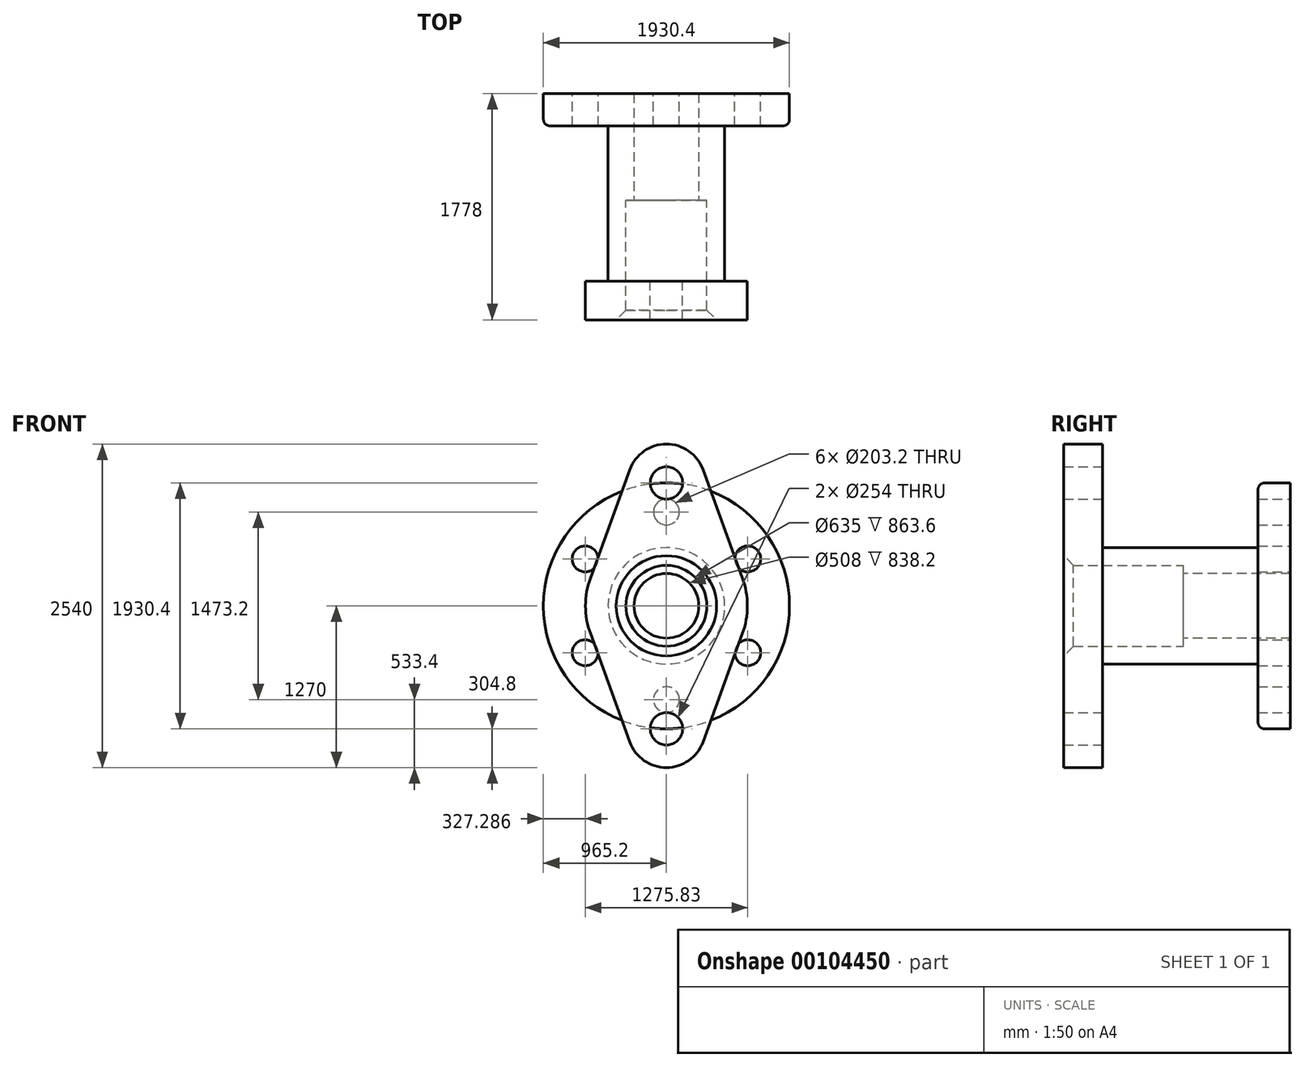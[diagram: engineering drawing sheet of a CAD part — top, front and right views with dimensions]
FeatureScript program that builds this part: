
annotation { "Feature Type Name" : "Feature", "Feature Type Description" : "" }
export const myFeature = defineFeature(function(context is Context, id is Id, definition is map)
    precondition{}
    {
        {
            var Q0;
            Q0=qCreatedBy(makeId("Front.planeOp"),FACE);
            var sketch = newSketch(context, id + "F0", { "sketchPlane" : qUnion([Q0])});
            skCircle(sketch, "E0", {"center": v(0, 0) * mm, "radius": 965.2 * mm});
            skCircle(sketch, "E1", {"center": v(0, 0) * mm, "radius": 736.6 * mm});
            skCircle(sketch, "E2", {"center": v(0, 736.6) * mm, "radius": 101.6 * mm});
            skCircle(sketch, "E3.1.0", {"center": v(-637.91, 368.3) * mm, "radius": 101.6 * mm});
            skCircle(sketch, "E3.2.0", {"center": v(-637.91, -368.3) * mm, "radius": 101.6 * mm});
            skCircle(sketch, "E3.3.0", {"center": v(0, -736.6) * mm, "radius": 101.6 * mm});
            skCircle(sketch, "E3.4.0", {"center": v(637.91, -368.3) * mm, "radius": 101.6 * mm});
            skCircle(sketch, "E3.5.0", {"center": v(637.91, 368.3) * mm, "radius": 101.6 * mm});
            skSolve(sketch);
        }
        {
            var Q0;
            Q0=qSketchRegion(id+"F0",true);
            var Q1;
            {var subQ1=sQuery(id+"F0.wireOp",EDGE,"E1");var subQ4=sQuery(id+"F0.wireOp",EDGE,"E3.7.0");var subQ22=makeQuery(id+"F0.imprint","INTERSECT",VERTEX,{"disambiguationData":[OD(0.0)],"derivedFrom":[subQ1,subQ4]});Q1=makeQuery(id+"F0.imprint","IMPRINT",FACE,{"disambiguationData":[TD([[makeQuery(id+"F0.imprint","IMPRINT",EDGE,{"disambiguationData":[TD([[subQ22,1.0]])],"derivedFrom":subQ1}),1.0]])]});}
            var Q2;
            {var subQ0=sQuery(id+"F0.wireOp",EDGE,"E3.1.0");var subQ1=sQuery(id+"F0.wireOp",EDGE,"E1");var subQ2=makeQuery(id+"F0.imprint","INTERSECT",VERTEX,{"disambiguationData":[OD(0.0)],"derivedFrom":[subQ1,subQ0]});Q2=makeQuery(id+"F0.imprint","IMPRINT",FACE,{"disambiguationData":[TD([[makeQuery(id+"F0.imprint","IMPRINT",EDGE,{"disambiguationData":[TD([[subQ2,-1.0]])],"derivedFrom":subQ1}),-1.0]])]});}
            var Q3;
            {var subQ0=sQuery(id+"F0.wireOp",EDGE,"E3.1.0");var subQ1=sQuery(id+"F0.wireOp",EDGE,"E1");var subQ2=makeQuery(id+"F0.imprint","INTERSECT",VERTEX,{"disambiguationData":[OD(0.0)],"derivedFrom":[subQ1,subQ0]});Q3=makeQuery(id+"F0.imprint","IMPRINT",FACE,{"disambiguationData":[TD([[makeQuery(id+"F0.imprint","IMPRINT",EDGE,{"disambiguationData":[TD([[subQ2,-1.0]])],"derivedFrom":subQ1}),1.0]])]});}
            var Q4;
            {var subQ0=sQuery(id+"F0.wireOp",EDGE,"E2");var subQ1=sQuery(id+"F0.wireOp",EDGE,"E1");var subQ2=makeQuery(id+"F0.imprint","INTERSECT",VERTEX,{"disambiguationData":[OD(0.0)],"derivedFrom":[subQ1,subQ0]});Q4=makeQuery(id+"F0.imprint","IMPRINT",FACE,{"disambiguationData":[TD([[makeQuery(id+"F0.imprint","IMPRINT",EDGE,{"disambiguationData":[TD([[subQ2,-1.0]])],"derivedFrom":subQ1}),-1.0]])]});}
            var Q5;
            {var subQ0=sQuery(id+"F0.wireOp",EDGE,"E2");var subQ1=sQuery(id+"F0.wireOp",EDGE,"E1");var subQ2=makeQuery(id+"F0.imprint","INTERSECT",VERTEX,{"disambiguationData":[OD(0.0)],"derivedFrom":[subQ1,subQ0]});Q5=makeQuery(id+"F0.imprint","IMPRINT",FACE,{"disambiguationData":[TD([[makeQuery(id+"F0.imprint","IMPRINT",EDGE,{"disambiguationData":[TD([[subQ2,-1.0]])],"derivedFrom":subQ1}),1.0]])]});}
            var Q6;
            {var subQ0=sQuery(id+"F0.wireOp",EDGE,"E3.7.0");var subQ1=sQuery(id+"F0.wireOp",EDGE,"E1");var subQ2=makeQuery(id+"F0.imprint","INTERSECT",VERTEX,{"disambiguationData":[OD(0.0)],"derivedFrom":[subQ1,subQ0]});Q6=makeQuery(id+"F0.imprint","IMPRINT",FACE,{"disambiguationData":[TD([[makeQuery(id+"F0.imprint","IMPRINT",EDGE,{"disambiguationData":[TD([[subQ2,-1.0]])],"derivedFrom":subQ1}),-1.0]])]});}
            var Q7;
            {var subQ0=sQuery(id+"F0.wireOp",EDGE,"E3.7.0");var subQ1=sQuery(id+"F0.wireOp",EDGE,"E1");var subQ2=makeQuery(id+"F0.imprint","INTERSECT",VERTEX,{"disambiguationData":[OD(0.0)],"derivedFrom":[subQ1,subQ0]});Q7=makeQuery(id+"F0.imprint","IMPRINT",FACE,{"disambiguationData":[TD([[makeQuery(id+"F0.imprint","IMPRINT",EDGE,{"disambiguationData":[TD([[subQ2,-1.0]])],"derivedFrom":subQ1}),1.0]])]});}
            var Q8;
            {var subQ0=sQuery(id+"F0.wireOp",EDGE,"E3.6.0");var subQ1=sQuery(id+"F0.wireOp",EDGE,"E1");var subQ2=makeQuery(id+"F0.imprint","INTERSECT",VERTEX,{"disambiguationData":[OD(0.0)],"derivedFrom":[subQ1,subQ0]});Q8=makeQuery(id+"F0.imprint","IMPRINT",FACE,{"disambiguationData":[TD([[makeQuery(id+"F0.imprint","IMPRINT",EDGE,{"disambiguationData":[TD([[subQ2,1.0]])],"derivedFrom":subQ1}),-1.0]])]});}
            var Q9;
            {var subQ0=sQuery(id+"F0.wireOp",EDGE,"E3.6.0");var subQ1=sQuery(id+"F0.wireOp",EDGE,"E1");var subQ2=makeQuery(id+"F0.imprint","INTERSECT",VERTEX,{"disambiguationData":[OD(0.0)],"derivedFrom":[subQ1,subQ0]});Q9=makeQuery(id+"F0.imprint","IMPRINT",FACE,{"disambiguationData":[TD([[makeQuery(id+"F0.imprint","IMPRINT",EDGE,{"disambiguationData":[TD([[subQ2,1.0]])],"derivedFrom":subQ1}),1.0]])]});}
            var Q10;
            {var subQ0=sQuery(id+"F0.wireOp",EDGE,"E3.2.0");var subQ1=sQuery(id+"F0.wireOp",EDGE,"E1");var subQ2=makeQuery(id+"F0.imprint","INTERSECT",VERTEX,{"disambiguationData":[OD(0.0)],"derivedFrom":[subQ1,subQ0]});Q10=makeQuery(id+"F0.imprint","IMPRINT",FACE,{"disambiguationData":[TD([[makeQuery(id+"F0.imprint","IMPRINT",EDGE,{"disambiguationData":[TD([[subQ2,-1.0]])],"derivedFrom":subQ1}),1.0]])]});}
            var Q11;
            {var subQ0=sQuery(id+"F0.wireOp",EDGE,"E3.2.0");var subQ1=sQuery(id+"F0.wireOp",EDGE,"E1");var subQ2=makeQuery(id+"F0.imprint","INTERSECT",VERTEX,{"disambiguationData":[OD(0.0)],"derivedFrom":[subQ1,subQ0]});Q11=makeQuery(id+"F0.imprint","IMPRINT",FACE,{"disambiguationData":[TD([[makeQuery(id+"F0.imprint","IMPRINT",EDGE,{"disambiguationData":[TD([[subQ2,-1.0]])],"derivedFrom":subQ1}),-1.0]])]});}
            var Q12;
            {var subQ0=sQuery(id+"F0.wireOp",EDGE,"E3.3.0");var subQ1=sQuery(id+"F0.wireOp",EDGE,"E1");var subQ2=makeQuery(id+"F0.imprint","INTERSECT",VERTEX,{"disambiguationData":[OD(0.0)],"derivedFrom":[subQ1,subQ0]});Q12=makeQuery(id+"F0.imprint","IMPRINT",FACE,{"disambiguationData":[TD([[makeQuery(id+"F0.imprint","IMPRINT",EDGE,{"disambiguationData":[TD([[subQ2,-1.0]])],"derivedFrom":subQ1}),-1.0]])]});}
            var Q13;
            {var subQ0=sQuery(id+"F0.wireOp",EDGE,"E3.3.0");var subQ1=sQuery(id+"F0.wireOp",EDGE,"E1");var subQ2=makeQuery(id+"F0.imprint","INTERSECT",VERTEX,{"disambiguationData":[OD(0.0)],"derivedFrom":[subQ1,subQ0]});Q13=makeQuery(id+"F0.imprint","IMPRINT",FACE,{"disambiguationData":[TD([[makeQuery(id+"F0.imprint","IMPRINT",EDGE,{"disambiguationData":[TD([[subQ2,-1.0]])],"derivedFrom":subQ1}),1.0]])]});}
            var Q14;
            {var subQ0=sQuery(id+"F0.wireOp",EDGE,"E3.4.0");var subQ1=sQuery(id+"F0.wireOp",EDGE,"E1");var subQ2=makeQuery(id+"F0.imprint","INTERSECT",VERTEX,{"disambiguationData":[OD(0.0)],"derivedFrom":[subQ1,subQ0]});Q14=makeQuery(id+"F0.imprint","IMPRINT",FACE,{"disambiguationData":[TD([[makeQuery(id+"F0.imprint","IMPRINT",EDGE,{"disambiguationData":[TD([[subQ2,-1.0]])],"derivedFrom":subQ1}),-1.0]])]});}
            var Q15;
            {var subQ0=sQuery(id+"F0.wireOp",EDGE,"E3.4.0");var subQ1=sQuery(id+"F0.wireOp",EDGE,"E1");var subQ2=makeQuery(id+"F0.imprint","INTERSECT",VERTEX,{"disambiguationData":[OD(0.0)],"derivedFrom":[subQ1,subQ0]});Q15=makeQuery(id+"F0.imprint","IMPRINT",FACE,{"disambiguationData":[TD([[makeQuery(id+"F0.imprint","IMPRINT",EDGE,{"disambiguationData":[TD([[subQ2,-1.0]])],"derivedFrom":subQ1}),1.0]])]});}
            var Q16;
            {var subQ0=sQuery(id+"F0.wireOp",EDGE,"E3.5.0");var subQ1=sQuery(id+"F0.wireOp",EDGE,"E1");var subQ2=makeQuery(id+"F0.imprint","INTERSECT",VERTEX,{"disambiguationData":[OD(0.0)],"derivedFrom":[subQ1,subQ0]});Q16=makeQuery(id+"F0.imprint","IMPRINT",FACE,{"disambiguationData":[TD([[makeQuery(id+"F0.imprint","IMPRINT",EDGE,{"disambiguationData":[TD([[subQ2,-1.0]])],"derivedFrom":subQ1}),-1.0]])]});}
            var Q17;
            {var subQ0=sQuery(id+"F0.wireOp",EDGE,"E3.5.0");var subQ1=sQuery(id+"F0.wireOp",EDGE,"E1");var subQ2=makeQuery(id+"F0.imprint","INTERSECT",VERTEX,{"disambiguationData":[OD(0.0)],"derivedFrom":[subQ1,subQ0]});Q17=makeQuery(id+"F0.imprint","IMPRINT",FACE,{"disambiguationData":[TD([[makeQuery(id+"F0.imprint","IMPRINT",EDGE,{"disambiguationData":[TD([[subQ2,-1.0]])],"derivedFrom":subQ1}),1.0]])]});}
            var Q18;
            {var subQ0=sQuery(id+"F0.wireOp",EDGE,"E3.5.0");var subQ1=sQuery(id+"F0.wireOp",EDGE,"E1");var subQ2=makeQuery(id+"F0.imprint","INTERSECT",VERTEX,{"disambiguationData":[OD(0.0)],"derivedFrom":[subQ1,subQ0]});Q18=makeQuery(id+"F0.imprint","IMPRINT",FACE,{"disambiguationData":[TD([[makeQuery(id+"F0.imprint","IMPRINT",EDGE,{"disambiguationData":[TD([[subQ2,1.0]])],"derivedFrom":subQ1}),1.0]])]});}
            var Q19;
            {var subQ0=sQuery(id+"F0.wireOp",EDGE,"E3.5.0");var subQ1=sQuery(id+"F0.wireOp",EDGE,"E1");var subQ2=makeQuery(id+"F0.imprint","INTERSECT",VERTEX,{"disambiguationData":[OD(0.0)],"derivedFrom":[subQ1,subQ0]});Q19=makeQuery(id+"F0.imprint","IMPRINT",FACE,{"disambiguationData":[TD([[makeQuery(id+"F0.imprint","IMPRINT",EDGE,{"disambiguationData":[TD([[subQ2,1.0]])],"derivedFrom":subQ1}),-1.0]])]});}
            extrude(context, id + "F1", {"entities" : qUnion([Q0, Q1, Q2, Q3, Q4, Q5, Q6, Q7, Q8, Q9, Q10, Q11, Q12, Q13, Q14, Q15, Q16, Q17, Q18, Q19]), "depth" : 254 * mm});
        }
        {
            var Q0;
            Q0=sQuery(id+"F0.wireOp",VERTEX,"E2.center");
            var Q1;
            Q1=sQuery(id+"F0.wireOp",VERTEX,"E3.1.0.center");
            var Q2;
            Q2=sQuery(id+"F0.wireOp",VERTEX,"E3.2.0.center");
            var Q3;
            Q3=sQuery(id+"F0.wireOp",VERTEX,"E3.3.0.center");
            var Q4;
            Q4=sQuery(id+"F0.wireOp",VERTEX,"E3.4.0.center");
            var Q5;
            Q5=sQuery(id+"F0.wireOp",VERTEX,"E3.5.0.center");
            var Q6;
            Q6=makeQuery(id+"F1.opExtrude","SWEPT_BODY",BODY,{"disambiguationData":[OSD([sQuery(id+"F0.wireOp",EDGE,"E0")])]});
            hole(context, id + "F2", {"style" : HoleStyle.SIMPLE, "endStyle" : HoleEndStyle.THROUGH, "oppositeDirection" : true, "holeDiameter" : 203.2 * mm, "locations" : qUnion([Q0, Q1, Q2, Q3, Q4, Q5]), "scope" : qUnion([Q6]), "isTappedThrough" : true});
        }
        {
            var Q0;
            Q0=makeQuery(id+"F1.opExtrude","CAP_FACE",FACE,{"disambiguationData":[OSD([sQuery(id+"F0.wireOp",EDGE,"E0")])],"isStart":false});
            var sketch = newSketch(context, id + "F3", { "sketchPlane" : qUnion([Q0])});
            skCircle(sketch, "E4", {"center": v(0, 0) * mm, "radius": 457.2 * mm});
            skCircle(sketch, "E5", {"center": v(0, 0) * mm, "radius": 254 * mm});
            skCircle(sketch, "E6", {"center": v(0, 0) * mm, "radius": 317.5 * mm});
            skSolve(sketch);
        }
        {
            var Q0;
            Q0=makeQuery(id+"F3.imprint","IMPRINT",FACE,{"disambiguationData":[TD([[makeQuery(id+"F3.imprint","IMPRINT",EDGE,{"derivedFrom":sQuery(id+"F3.wireOp",EDGE,"E4")}),1.0]])]});
            extrude(context, id + "F4", {"entities" : qUnion([Q0]), "operationType" : NewBodyOperationType.ADD, "depth" : 1219.2 * mm});
        }
        {
            var Q0;
            Q0=makeQuery(id+"F1.opExtrude","CAP_EDGE",EDGE,{"disambiguationData":[OSD([sQuery(id+"F0.wireOp",EDGE,"E0")])],"isStart":false});
            var Q1;
            Q1=makeQuery(id+"F4.opExtrude","CAP_EDGE",EDGE,{"disambiguationData":[OSD([sQuery(id+"F3.wireOp",EDGE,"E4")])],"isStart":true});
            fillet(context, id + "F5", {"entities" : qUnion([Q0, Q1]), "radius" : 50.8 * mm, "tangentPropagation" : true, "allowEdgeOverflow" : false});
        }
        {
            var Q0;
            Q0=makeQuery(id+"F3.imprint","IMPRINT",FACE,{"disambiguationData":[TD([[makeQuery(id+"F3.imprint","IMPRINT",EDGE,{"derivedFrom":sQuery(id+"F3.wireOp",EDGE,"E5")}),1.0]])]});
            extrude(context, id + "F6", {"entities" : qUnion([Q0]), "operationType" : NewBodyOperationType.REMOVE, "endBound" : BoundingType.THROUGH_ALL, "oppositeDirection" : true, "depth" : 2540 * mm});
        }
        {
            var Q0;
            Q0=makeQuery(id+"F3.imprint","IMPRINT",FACE,{"disambiguationData":[TD([[makeQuery(id+"F3.imprint","IMPRINT",EDGE,{"derivedFrom":sQuery(id+"F3.wireOp",EDGE,"E5")}),-1.0]])]});
            extrude(context, id + "F7", {"entities" : qUnion([Q0]), "operationType" : NewBodyOperationType.ADD, "depth" : 584.2 * mm});
        }
        {
            var Q0;
            Q0=makeQuery(id+"F4.opExtrude","CAP_FACE",FACE,{"disambiguationData":[OSD([sQuery(id+"F3.wireOp",EDGE,"E4"),sQuery(id+"F3.wireOp",EDGE,"E6")])],"isStart":false});
            var sketch = newSketch(context, id + "F8", { "sketchPlane" : qUnion([Q0])});
            skLineSegment(sketch, "E7", {"start": v(0, 0) * mm, "end": v(0, 2027.99) * mm});
            skLineSegment(sketch, "E8", {"start": v(0, 0) * mm, "end": v(0, -1830.79) * mm});
            skLineSegment(sketch, "E9", {"start": v(0, 0) * mm, "end": v(-1579.68, 0) * mm});
            skLineSegment(sketch, "E10", {"start": v(0, 0) * mm, "end": v(2023.02, 0) * mm});
            skSolve(sketch);
        }
        {
            var Q0;
            {var subQ0=sQuery(id+"F8.wireOp",EDGE,"E7");var subQ1=makeQuery(id+"F4.opExtrude","CAP_EDGE",EDGE,{"disambiguationData":[OSD([sQuery(id+"F3.wireOp",EDGE,"E4")])],"isStart":false});var subQ2=makeQuery(id+"F8.imprint","INTERSECT",VERTEX,{"derivedFrom":[subQ1,subQ0]});Q0=makeQuery(id+"F8.imprint","IMPRINT",FACE,{"disambiguationData":[TD([[makeQuery(id+"F8.imprint","IMPRINT",EDGE,{"disambiguationData":[TD([[subQ2,1.0]])],"derivedFrom":subQ0}),1.0]])]});}
            var sketch = newSketch(context, id + "F9", { "sketchPlane" : qUnion([Q0])});
            skPoint(sketch, "E11", {"position": v(0, 965.2) * mm});
            skPoint(sketch, "E12", {"position": v(0, -965.2) * mm});
            skCircle(sketch, "E13", {"center": v(0, 965.2) * mm, "radius": 304.8 * mm});
            skCircle(sketch, "E14", {"center": v(0, 965.2) * mm, "radius": 127 * mm});
            skCircle(sketch, "E15", {"center": v(0, -965.2) * mm, "radius": 304.8 * mm});
            skCircle(sketch, "E16", {"center": v(0, -965.2) * mm, "radius": 127 * mm});
            skCircle(sketch, "E17", {"center": v(0, 0) * mm, "radius": 279.4 * mm});
            skCircle(sketch, "E18", {"center": v(0, 0) * mm, "radius": 330.2 * mm});
            skCircle(sketch, "E19", {"center": v(0, 0) * mm, "radius": 635 * mm});
            skLineSegment(sketch, "E20", {"start": v(286.4, 1069.47) * mm, "end": v(597.58, 214.77) * mm});
            skLineSegment(sketch, "E21", {"start": v(596.69, -217.24) * mm, "end": v(248.85, -1172.62) * mm});
            skLineSegment(sketch, "E22", {"start": v(0, 965.2) * mm, "end": v(0, -965.2) * mm});
            skLineSegment(sketch, "E23", {"start": v(-286.4, -1069.47) * mm, "end": v(-675.78, 0) * mm});
            skLineSegment(sketch, "E24", {"start": v(-286.4, 1069.47) * mm, "end": v(-596.69, 217.24) * mm});
            skSolve(sketch);
        }
        {
            var Q0;
            {var subQ13=sQuery(id+"F9.wireOp",EDGE,"ya8A9BkE-coIV-0aEf-c29y-W11fJcQt8qWr");Q0=makeQuery(id+"F9.imprint","IMPRINT",FACE,{"disambiguationData":[TD([[makeQuery(id+"F9.imprint","IMPRINT",EDGE,{"derivedFrom":subQ13}),-1.0]])]});}
            var Q1;
            {var subQ1=sQuery(id+"F8.wireOp",EDGE,"E7");var subQ2=makeQuery(id+"F4.opExtrude","CAP_EDGE",EDGE,{"disambiguationData":[OSD([sQuery(id+"F3.wireOp",EDGE,"E4")])],"isStart":false});var subQ3=makeQuery(id+"F8.imprint","INTERSECT",VERTEX,{"derivedFrom":[subQ2,subQ1]});var subQ11=makeQuery(id+"F8.imprint","IMPRINT",EDGE,{"disambiguationData":[TD([[subQ3,-1.0]])],"derivedFrom":subQ2});Q1=makeQuery(id+"F9.imprint","IMPRINT",FACE,{"disambiguationData":[TD([[makeQuery(id+"F9.imprint","IMPRINT",EDGE,{"derivedFrom":subQ11}),1.0]])]});}
            var Q2;
            Q2=makeQuery(id+"F9.imprint","IMPRINT",FACE,{"disambiguationData":[TD([[makeQuery(id+"F9.imprint","IMPRINT",EDGE,{"derivedFrom":sQuery(id+"F9.wireOp",EDGE,"E16")}),-1.0]])]});
            var Q3;
            {var subQ0=sQuery(id+"F9.wireOp",EDGE,"qZcp2iFD-yTbO-aO5D-vJsB-K42KSH7r9xvT");var subQ1=makeQuery(id+"F9.imprint","INTERSECT",VERTEX,{"derivedFrom":[subQ0,sQuery(id+"F9.wireOp",EDGE,"eW8BNkMa-DnNI-QZdu-Olqy-l7O4oWZxZ6XR")]});Q3=makeQuery(id+"F9.imprint","IMPRINT",FACE,{"disambiguationData":[TD([[makeQuery(id+"F9.imprint","IMPRINT",EDGE,{"disambiguationData":[TD([[subQ1,-1.0]])],"derivedFrom":subQ0}),1.0]])]});}
            var Q4;
            {var subQ0=sQuery(id+"F9.wireOp",EDGE,"h6m9uejH-BYQN-DJct-PYJt-bV2pgaKJldlE");var subQ1=makeQuery(id+"F9.imprint","INTERSECT",VERTEX,{"derivedFrom":[subQ0,sQuery(id+"F9.wireOp",EDGE,"ya8A9BkE-coIV-0aEf-c29y-W11fJcQt8qWr")]});Q4=makeQuery(id+"F9.imprint","IMPRINT",FACE,{"disambiguationData":[TD([[makeQuery(id+"F9.imprint","IMPRINT",EDGE,{"disambiguationData":[TD([[subQ1,-1.0]])],"derivedFrom":subQ0}),1.0]])]});}
            var Q5;
            Q5=makeQuery(id+"F9.imprint","IMPRINT",FACE,{"disambiguationData":[TD([[makeQuery(id+"F9.imprint","IMPRINT",EDGE,{"derivedFrom":sQuery(id+"F9.wireOp",EDGE,"E14")}),-1.0]])]});
            var Q6;
            {var subQ0=sQuery(id+"F9.wireOp",EDGE,"E24");Q6=makeQuery(id+"F9.imprint","IMPRINT",FACE,{"disambiguationData":[TD([[makeQuery(id+"F9.imprint","IMPRINT",EDGE,{"derivedFrom":subQ0}),1.0]])]});}
            var Q7;
            {var subQ0=sQuery(id+"F9.wireOp",EDGE,"E19");var subQ4=makeQuery(id+"F9.imprint","INTERSECT",VERTEX,{"derivedFrom":[subQ0,sQuery(id+"F9.wireOp",EDGE,"E24")]});Q7=makeQuery(id+"F9.imprint","IMPRINT",FACE,{"disambiguationData":[TD([[makeQuery(id+"F9.imprint","IMPRINT",EDGE,{"disambiguationData":[TD([[subQ4,1.0]])],"derivedFrom":subQ0}),1.0]])]});}
            var Q8;
            {var subQ0=sQuery(id+"F9.wireOp",EDGE,"E20");var subQ1=sQuery(id+"F9.wireOp",EDGE,"E13");var subQ2=makeQuery(id+"F9.imprint","INTERSECT",VERTEX,{"derivedFrom":[subQ1,subQ0]});Q8=makeQuery(id+"F9.imprint","IMPRINT",FACE,{"disambiguationData":[TD([[makeQuery(id+"F9.imprint","IMPRINT",EDGE,{"disambiguationData":[TD([[subQ2,1.0]])],"derivedFrom":subQ1}),-1.0]])]});}
            var Q9;
            {var subQ3=sQuery(id+"F9.wireOp",EDGE,"E22");var subQ6=sQuery(id+"F9.wireOp",EDGE,"E18");var subQ7=makeQuery(id+"F9.imprint","INTERSECT",VERTEX,{"disambiguationData":[OD(0.0)],"derivedFrom":[subQ6,subQ3]});Q9=makeQuery(id+"F9.imprint","IMPRINT",FACE,{"disambiguationData":[TD([[makeQuery(id+"F9.imprint","IMPRINT",EDGE,{"disambiguationData":[TD([[subQ7,1.0]])],"derivedFrom":subQ6}),-1.0]])]});}
            var Q10;
            {var subQ0=sQuery(id+"F9.wireOp",EDGE,"E21");var subQ1=sQuery(id+"F9.wireOp",EDGE,"E15");var subQ2=makeQuery(id+"F9.imprint","INTERSECT",VERTEX,{"derivedFrom":[subQ1,subQ0]});Q10=makeQuery(id+"F9.imprint","IMPRINT",FACE,{"disambiguationData":[TD([[makeQuery(id+"F9.imprint","IMPRINT",EDGE,{"disambiguationData":[TD([[subQ2,-1.0]])],"derivedFrom":subQ1}),-1.0]])]});}
            var Q11;
            {var subQ0=sQuery(id+"F9.wireOp",EDGE,"E23");var subQ1=sQuery(id+"F9.wireOp",EDGE,"E15");var subQ2=makeQuery(id+"F9.imprint","INTERSECT",VERTEX,{"derivedFrom":[subQ1,subQ0]});Q11=makeQuery(id+"F9.imprint","IMPRINT",FACE,{"disambiguationData":[TD([[makeQuery(id+"F9.imprint","IMPRINT",EDGE,{"disambiguationData":[TD([[subQ2,1.0]])],"derivedFrom":subQ1}),-1.0]])]});}
            extrude(context, id + "F10", {"entities" : qUnion([Q0, Q1, Q2, Q3, Q4, Q5, Q6, Q7, Q8, Q9, Q10, Q11]), "operationType" : NewBodyOperationType.ADD, "depth" : 304.8 * mm});
        }
        {
            var Q0;
            {var subQ0=sQuery(id+"F8.wireOp",EDGE,"E8");var subQ1=makeQuery(id+"F4.opExtrude","CAP_EDGE",EDGE,{"disambiguationData":[OSD([sQuery(id+"F3.wireOp",EDGE,"E4")])],"isStart":false});var subQ2=makeQuery(id+"F8.imprint","INTERSECT",VERTEX,{"derivedFrom":[subQ1,subQ0]});Q0=makeQuery(id+"F8.imprint","IMPRINT",FACE,{"disambiguationData":[TD([[makeQuery(id+"F8.imprint","IMPRINT",EDGE,{"disambiguationData":[TD([[subQ2,1.0]])],"derivedFrom":subQ0}),-1.0]])]});}
            var Q1;
            {var subQ0=sQuery(id+"F8.wireOp",EDGE,"E7");var subQ1=makeQuery(id+"F4.opExtrude","CAP_EDGE",EDGE,{"disambiguationData":[OSD([sQuery(id+"F3.wireOp",EDGE,"E4")])],"isStart":false});var subQ2=makeQuery(id+"F8.imprint","INTERSECT",VERTEX,{"derivedFrom":[subQ1,subQ0]});Q1=makeQuery(id+"F8.imprint","IMPRINT",FACE,{"disambiguationData":[TD([[makeQuery(id+"F8.imprint","IMPRINT",EDGE,{"disambiguationData":[TD([[subQ2,1.0]])],"derivedFrom":subQ0}),1.0]])]});}
            var Q2;
            {var subQ0=sQuery(id+"F8.wireOp",EDGE,"E7");var subQ1=makeQuery(id+"F4.opExtrude","CAP_EDGE",EDGE,{"disambiguationData":[OSD([sQuery(id+"F3.wireOp",EDGE,"E4")])],"isStart":false});var subQ2=makeQuery(id+"F8.imprint","INTERSECT",VERTEX,{"derivedFrom":[subQ1,subQ0]});Q2=makeQuery(id+"F8.imprint","IMPRINT",FACE,{"disambiguationData":[TD([[makeQuery(id+"F8.imprint","IMPRINT",EDGE,{"disambiguationData":[TD([[subQ2,1.0]])],"derivedFrom":subQ0}),-1.0]])]});}
            var Q3;
            {var subQ0=sQuery(id+"F8.wireOp",EDGE,"E8");var subQ1=makeQuery(id+"F4.opExtrude","CAP_EDGE",EDGE,{"disambiguationData":[OSD([sQuery(id+"F3.wireOp",EDGE,"E4")])],"isStart":false});var subQ2=makeQuery(id+"F8.imprint","INTERSECT",VERTEX,{"derivedFrom":[subQ1,subQ0]});Q3=makeQuery(id+"F8.imprint","IMPRINT",FACE,{"disambiguationData":[TD([[makeQuery(id+"F8.imprint","IMPRINT",EDGE,{"disambiguationData":[TD([[subQ2,1.0]])],"derivedFrom":subQ0}),1.0]])]});}
            extrude(context, id + "F11", {"entities" : qUnion([Q0, Q1, Q2, Q3]), "operationType" : NewBodyOperationType.ADD, "depth" : 304.8 * mm});
        }
        {
            var Q0;
            Q0=makeQuery(id+"F11.opExtrude","CAP_EDGE",EDGE,{"disambiguationData":[OSD([sQuery(id+"F3.wireOp",EDGE,"E6")])],"isStart":false});
            chamfer(context, id + "F12", {"entities" : qUnion([Q0]), "chamferType" : ChamferType.OFFSET_ANGLE, "width" : 76.2 * mm, "oppositeDirection" : false, "angle" : 45 * degree, "tangentPropagation" : true});
        }
    });
